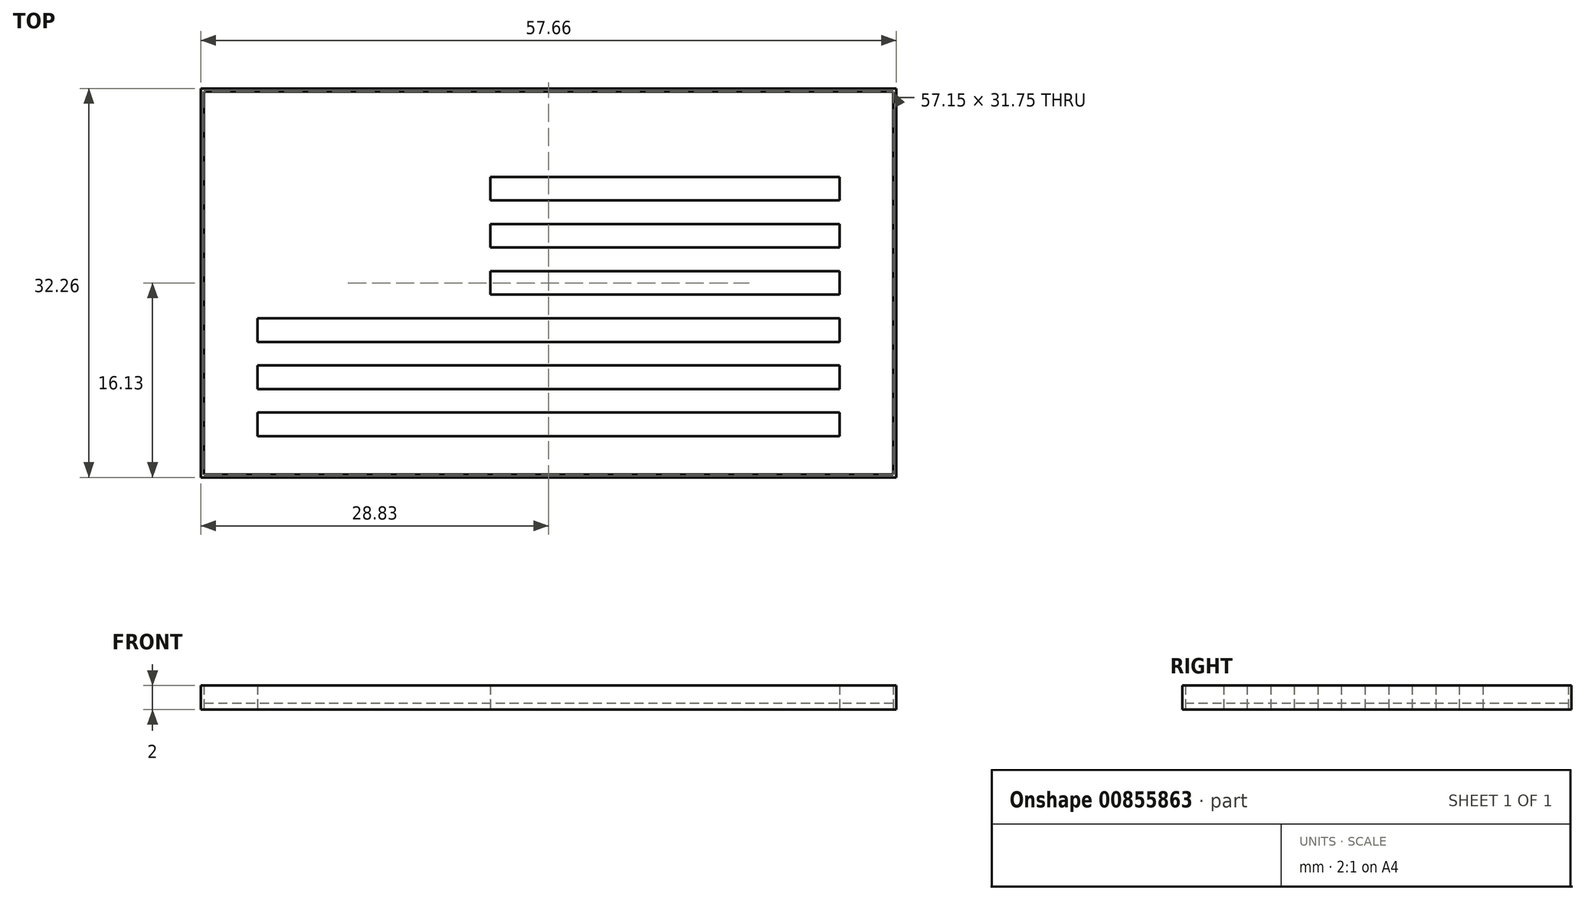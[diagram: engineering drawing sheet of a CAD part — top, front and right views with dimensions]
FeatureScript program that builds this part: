
annotation { "Feature Type Name" : "Feature", "Feature Type Description" : "" }
export const myFeature = defineFeature(function(context is Context, id is Id, definition is map)
    precondition{}
    {
        {
            var Q0;
            Q0=qCreatedBy(makeId("Top.planeOp"),FACE);
            var sketch = newSketch(context, id + "F0", { "sketchPlane" : qUnion([Q0])});
            skLineSegment(sketch, "E0.rect.bottom", {"start": v(24.13, 12.7) * mm, "end": v(-24.13, 12.7) * mm});
            skLineSegment(sketch, "E0.rect.top", {"start": v(24.13, -12.7) * mm, "end": v(-24.13, -12.7) * mm});
            skLineSegment(sketch, "E0.rect.left", {"start": v(24.13, 12.7) * mm, "end": v(24.13, -12.7) * mm});
            skLineSegment(sketch, "E0.rect.right", {"start": v(-24.13, 12.7) * mm, "end": v(-24.13, -12.7) * mm});
            skPoint(sketch, "E0.rect.middle", {"position": v(0, 0) * mm});
            skLineSegment(sketch, "E1.bottom", {"start": v(-24.13, 12.7) * mm, "end": v(-4.83, 12.7) * mm});
            skLineSegment(sketch, "E1.top", {"start": v(-24.13, -0.98) * mm, "end": v(-4.83, -0.98) * mm});
            skLineSegment(sketch, "E1.left", {"start": v(-24.13, 12.7) * mm, "end": v(-24.13, -0.98) * mm});
            skLineSegment(sketch, "E1.right", {"start": v(-4.83, 12.7) * mm, "end": v(-4.83, -0.98) * mm});
            skLineSegment(sketch, "E2.bottom", {"start": v(-4.83, 12.7) * mm, "end": v(24.13, 12.7) * mm});
            skLineSegment(sketch, "E2.top", {"start": v(-4.83, 10.75) * mm, "end": v(24.13, 10.75) * mm});
            skLineSegment(sketch, "E2.left", {"start": v(-4.83, 12.7) * mm, "end": v(-4.83, 10.75) * mm});
            skLineSegment(sketch, "E2.right", {"start": v(24.13, 12.7) * mm, "end": v(24.13, 10.75) * mm});
            skLineSegment(sketch, "E3.MirrorCS", {"start": v(-4.83, 8.8) * mm, "end": v(24.13, 8.8) * mm});
            skLineSegment(sketch, "E4.MirrorCS", {"start": v(-4.83, 6.84) * mm, "end": v(24.13, 6.84) * mm});
            skLineSegment(sketch, "E5.MirrorCS", {"start": v(-4.83, 4.89) * mm, "end": v(24.13, 4.89) * mm});
            skLineSegment(sketch, "E6.MirrorCS", {"start": v(-4.83, 2.93) * mm, "end": v(24.13, 2.93) * mm});
            skLineSegment(sketch, "E7.MirrorCS", {"start": v(-4.83, 0.98) * mm, "end": v(24.13, 0.98) * mm});
            skLineSegment(sketch, "E8.MirrorCS", {"start": v(-4.83, -0.97) * mm, "end": v(24.13, -0.97) * mm});
            skLineSegment(sketch, "E9.bottom", {"start": v(-24.13, -0.98) * mm, "end": v(24.13, -0.98) * mm});
            skLineSegment(sketch, "E9.top", {"start": v(-24.13, -2.93) * mm, "end": v(24.13, -2.93) * mm});
            skLineSegment(sketch, "E9.left", {"start": v(-24.13, -0.98) * mm, "end": v(-24.13, -2.93) * mm});
            skLineSegment(sketch, "E9.right", {"start": v(24.13, -0.98) * mm, "end": v(24.13, -2.93) * mm});
            skLineSegment(sketch, "E10.MirrorCS", {"start": v(-24.13, -4.88) * mm, "end": v(24.13, -4.88) * mm});
            skLineSegment(sketch, "E11.MirrorCS", {"start": v(-24.13, -6.84) * mm, "end": v(24.13, -6.84) * mm});
            skLineSegment(sketch, "E12.MirrorCS", {"start": v(-24.13, -8.8) * mm, "end": v(24.13, -8.8) * mm});
            skLineSegment(sketch, "E13.MirrorCS", {"start": v(-24.13, -10.74) * mm, "end": v(24.13, -10.74) * mm});
            skLineSegment(sketch, "E14.bottom", {"start": v(-24.13, 12.7) * mm, "end": v(-22.53, 12.7) * mm});
            skLineSegment(sketch, "E14.left", {"start": v(-24.13, 12.7) * mm, "end": v(-24.13, 11.33) * mm});
            skPoint(sketch, "E15.cCircle.perimeterSnap0", {"position": v(-22.53, 12.01) * mm});
            skPoint(sketch, "E15.0.startSnap0", {"position": v(-22.53, 12.01) * mm});
            skLineSegment(sketch, "E16", {"start": v(-22.53, 12.12) * mm, "end": v(-22.35, 11.57) * mm});
            skLineSegment(sketch, "E17", {"start": v(-21.78, 11.57) * mm, "end": v(-22.35, 11.57) * mm});
            skLineSegment(sketch, "E18", {"start": v(-23, 10.7) * mm, "end": v(-22.82, 11.24) * mm});
            skLineSegment(sketch, "E19", {"start": v(-23.28, 11.57) * mm, "end": v(-22.82, 11.24) * mm});
            skLineSegment(sketch, "E20", {"start": v(-21.78, 11.57) * mm, "end": v(-22.24, 11.24) * mm});
            skLineSegment(sketch, "E21.trimOffspring", {"start": v(-22.24, 11.24) * mm, "end": v(-22.07, 10.7) * mm});
            skLineSegment(sketch, "E22.trimOffspring", {"start": v(-22.53, 11.03) * mm, "end": v(-23, 10.7) * mm});
            skLineSegment(sketch, "E23.trimOffspring", {"start": v(-22.53, 11.03) * mm, "end": v(-22.07, 10.7) * mm});
            skLineSegment(sketch, "E24.trimOffspring", {"start": v(-22.7, 11.57) * mm, "end": v(-22.53, 12.12) * mm});
            skLineSegment(sketch, "E25.trimOffspring", {"start": v(-22.7, 11.57) * mm, "end": v(-23.28, 11.57) * mm});
            skLineSegment(sketch, "E26.0.1.0", {"start": v(-22.53, 9.37) * mm, "end": v(-22.35, 8.83) * mm});
            skLineSegment(sketch, "E26.0.1.1", {"start": v(-21.78, 8.83) * mm, "end": v(-22.35, 8.83) * mm});
            skLineSegment(sketch, "E26.0.1.2", {"start": v(-21.78, 8.83) * mm, "end": v(-22.24, 8.5) * mm});
            skLineSegment(sketch, "E26.0.1.3", {"start": v(-22.24, 8.5) * mm, "end": v(-22.07, 7.95) * mm});
            skLineSegment(sketch, "E26.0.1.4", {"start": v(-22.53, 8.28) * mm, "end": v(-22.07, 7.95) * mm});
            skLineSegment(sketch, "E26.0.1.5", {"start": v(-22.53, 8.28) * mm, "end": v(-23, 7.95) * mm});
            skLineSegment(sketch, "E26.0.1.6", {"start": v(-23, 7.95) * mm, "end": v(-22.82, 8.5) * mm});
            skLineSegment(sketch, "E26.0.1.7", {"start": v(-23.28, 8.83) * mm, "end": v(-22.82, 8.5) * mm});
            skLineSegment(sketch, "E26.0.1.8", {"start": v(-22.7, 8.83) * mm, "end": v(-22.53, 9.37) * mm});
            skLineSegment(sketch, "E26.0.1.9", {"start": v(-22.7, 8.83) * mm, "end": v(-23.28, 8.83) * mm});
            skLineSegment(sketch, "E26.0.2.0", {"start": v(-22.53, 6.63) * mm, "end": v(-22.35, 6.09) * mm});
            skLineSegment(sketch, "E26.0.2.1", {"start": v(-21.78, 6.09) * mm, "end": v(-22.35, 6.09) * mm});
            skLineSegment(sketch, "E26.0.2.2", {"start": v(-21.78, 6.09) * mm, "end": v(-22.24, 5.75) * mm});
            skLineSegment(sketch, "E26.0.2.3", {"start": v(-22.24, 5.75) * mm, "end": v(-22.07, 5.2) * mm});
            skLineSegment(sketch, "E26.0.2.4", {"start": v(-22.53, 5.54) * mm, "end": v(-22.07, 5.2) * mm});
            skLineSegment(sketch, "E26.0.2.5", {"start": v(-22.53, 5.54) * mm, "end": v(-23, 5.2) * mm});
            skLineSegment(sketch, "E26.0.2.6", {"start": v(-23, 5.2) * mm, "end": v(-22.82, 5.75) * mm});
            skLineSegment(sketch, "E26.0.2.7", {"start": v(-23.28, 6.09) * mm, "end": v(-22.82, 5.75) * mm});
            skLineSegment(sketch, "E26.0.2.8", {"start": v(-22.7, 6.09) * mm, "end": v(-22.53, 6.63) * mm});
            skLineSegment(sketch, "E26.0.2.9", {"start": v(-22.7, 6.09) * mm, "end": v(-23.28, 6.09) * mm});
            skLineSegment(sketch, "E26.0.3.0", {"start": v(-22.53, 3.89) * mm, "end": v(-22.35, 3.34) * mm});
            skLineSegment(sketch, "E26.0.3.1", {"start": v(-21.78, 3.34) * mm, "end": v(-22.35, 3.34) * mm});
            skLineSegment(sketch, "E26.0.3.2", {"start": v(-21.78, 3.34) * mm, "end": v(-22.24, 3) * mm});
            skLineSegment(sketch, "E26.0.3.3", {"start": v(-22.24, 3) * mm, "end": v(-22.07, 2.46) * mm});
            skLineSegment(sketch, "E26.0.3.4", {"start": v(-22.53, 2.8) * mm, "end": v(-22.07, 2.46) * mm});
            skLineSegment(sketch, "E26.0.3.5", {"start": v(-22.53, 2.8) * mm, "end": v(-23, 2.46) * mm});
            skLineSegment(sketch, "E26.0.3.6", {"start": v(-23, 2.46) * mm, "end": v(-22.82, 3) * mm});
            skLineSegment(sketch, "E26.0.3.7", {"start": v(-23.28, 3.34) * mm, "end": v(-22.82, 3) * mm});
            skLineSegment(sketch, "E26.0.3.8", {"start": v(-22.7, 3.34) * mm, "end": v(-22.53, 3.89) * mm});
            skLineSegment(sketch, "E26.0.3.9", {"start": v(-22.7, 3.34) * mm, "end": v(-23.28, 3.34) * mm});
            skLineSegment(sketch, "E26.0.4.0", {"start": v(-22.53, 1.14) * mm, "end": v(-22.35, 0.6) * mm});
            skLineSegment(sketch, "E26.0.4.1", {"start": v(-21.78, 0.6) * mm, "end": v(-22.35, 0.6) * mm});
            skLineSegment(sketch, "E26.0.4.2", {"start": v(-21.78, 0.6) * mm, "end": v(-22.24, 0.26) * mm});
            skLineSegment(sketch, "E26.0.4.3", {"start": v(-22.24, 0.26) * mm, "end": v(-22.07, -0.28) * mm});
            skLineSegment(sketch, "E26.0.4.4", {"start": v(-22.53, 0.05) * mm, "end": v(-22.07, -0.28) * mm});
            skLineSegment(sketch, "E26.0.4.5", {"start": v(-22.53, 0.05) * mm, "end": v(-23, -0.28) * mm});
            skLineSegment(sketch, "E26.0.4.6", {"start": v(-23, -0.28) * mm, "end": v(-22.82, 0.26) * mm});
            skLineSegment(sketch, "E26.0.4.7", {"start": v(-23.28, 0.6) * mm, "end": v(-22.82, 0.26) * mm});
            skLineSegment(sketch, "E26.0.4.8", {"start": v(-22.7, 0.6) * mm, "end": v(-22.53, 1.14) * mm});
            skLineSegment(sketch, "E26.0.4.9", {"start": v(-22.7, 0.6) * mm, "end": v(-23.28, 0.6) * mm});
            skLineSegment(sketch, "E26.1.0.0", {"start": v(-19.33, 12.12) * mm, "end": v(-19.15, 11.57) * mm});
            skLineSegment(sketch, "E26.1.0.1", {"start": v(-18.58, 11.57) * mm, "end": v(-19.15, 11.57) * mm});
            skLineSegment(sketch, "E26.1.0.2", {"start": v(-18.58, 11.57) * mm, "end": v(-19.04, 11.24) * mm});
            skLineSegment(sketch, "E26.1.0.3", {"start": v(-19.04, 11.24) * mm, "end": v(-18.87, 10.7) * mm});
            skLineSegment(sketch, "E26.1.0.4", {"start": v(-19.33, 11.03) * mm, "end": v(-18.87, 10.7) * mm});
            skLineSegment(sketch, "E26.1.0.5", {"start": v(-19.33, 11.03) * mm, "end": v(-19.8, 10.7) * mm});
            skLineSegment(sketch, "E26.1.0.6", {"start": v(-19.8, 10.7) * mm, "end": v(-19.62, 11.24) * mm});
            skLineSegment(sketch, "E26.1.0.7", {"start": v(-20.08, 11.57) * mm, "end": v(-19.62, 11.24) * mm});
            skLineSegment(sketch, "E26.1.0.8", {"start": v(-19.5, 11.57) * mm, "end": v(-19.33, 12.12) * mm});
            skLineSegment(sketch, "E26.1.0.9", {"start": v(-19.5, 11.57) * mm, "end": v(-20.08, 11.57) * mm});
            skLineSegment(sketch, "E26.1.1.0", {"start": v(-19.33, 9.37) * mm, "end": v(-19.15, 8.83) * mm});
            skLineSegment(sketch, "E26.1.1.1", {"start": v(-18.58, 8.83) * mm, "end": v(-19.15, 8.83) * mm});
            skLineSegment(sketch, "E26.1.1.2", {"start": v(-18.58, 8.83) * mm, "end": v(-19.04, 8.5) * mm});
            skLineSegment(sketch, "E26.1.1.3", {"start": v(-19.04, 8.5) * mm, "end": v(-18.87, 7.95) * mm});
            skLineSegment(sketch, "E26.1.1.4", {"start": v(-19.33, 8.28) * mm, "end": v(-18.87, 7.95) * mm});
            skLineSegment(sketch, "E26.1.1.5", {"start": v(-19.33, 8.28) * mm, "end": v(-19.8, 7.95) * mm});
            skLineSegment(sketch, "E26.1.1.6", {"start": v(-19.8, 7.95) * mm, "end": v(-19.62, 8.5) * mm});
            skLineSegment(sketch, "E26.1.1.7", {"start": v(-20.08, 8.83) * mm, "end": v(-19.62, 8.5) * mm});
            skLineSegment(sketch, "E26.1.1.8", {"start": v(-19.5, 8.83) * mm, "end": v(-19.33, 9.37) * mm});
            skLineSegment(sketch, "E26.1.1.9", {"start": v(-19.5, 8.83) * mm, "end": v(-20.08, 8.83) * mm});
            skLineSegment(sketch, "E26.1.2.0", {"start": v(-19.33, 6.63) * mm, "end": v(-19.15, 6.09) * mm});
            skLineSegment(sketch, "E26.1.2.1", {"start": v(-18.58, 6.09) * mm, "end": v(-19.15, 6.09) * mm});
            skLineSegment(sketch, "E26.1.2.2", {"start": v(-18.58, 6.09) * mm, "end": v(-19.04, 5.75) * mm});
            skLineSegment(sketch, "E26.1.2.3", {"start": v(-19.04, 5.75) * mm, "end": v(-18.87, 5.2) * mm});
            skLineSegment(sketch, "E26.1.2.4", {"start": v(-19.33, 5.54) * mm, "end": v(-18.87, 5.2) * mm});
            skLineSegment(sketch, "E26.1.2.5", {"start": v(-19.33, 5.54) * mm, "end": v(-19.8, 5.2) * mm});
            skLineSegment(sketch, "E26.1.2.6", {"start": v(-19.8, 5.2) * mm, "end": v(-19.62, 5.75) * mm});
            skLineSegment(sketch, "E26.1.2.7", {"start": v(-20.08, 6.09) * mm, "end": v(-19.62, 5.75) * mm});
            skLineSegment(sketch, "E26.1.2.8", {"start": v(-19.5, 6.09) * mm, "end": v(-19.33, 6.63) * mm});
            skLineSegment(sketch, "E26.1.2.9", {"start": v(-19.5, 6.09) * mm, "end": v(-20.08, 6.09) * mm});
            skLineSegment(sketch, "E26.1.3.0", {"start": v(-19.33, 3.89) * mm, "end": v(-19.15, 3.34) * mm});
            skLineSegment(sketch, "E26.1.3.1", {"start": v(-18.58, 3.34) * mm, "end": v(-19.15, 3.34) * mm});
            skLineSegment(sketch, "E26.1.3.2", {"start": v(-18.58, 3.34) * mm, "end": v(-19.04, 3) * mm});
            skLineSegment(sketch, "E26.1.3.3", {"start": v(-19.04, 3) * mm, "end": v(-18.87, 2.46) * mm});
            skLineSegment(sketch, "E26.1.3.4", {"start": v(-19.33, 2.8) * mm, "end": v(-18.87, 2.46) * mm});
            skLineSegment(sketch, "E26.1.3.5", {"start": v(-19.33, 2.8) * mm, "end": v(-19.8, 2.46) * mm});
            skLineSegment(sketch, "E26.1.3.6", {"start": v(-19.8, 2.46) * mm, "end": v(-19.62, 3) * mm});
            skLineSegment(sketch, "E26.1.3.7", {"start": v(-20.08, 3.34) * mm, "end": v(-19.62, 3) * mm});
            skLineSegment(sketch, "E26.1.3.8", {"start": v(-19.5, 3.34) * mm, "end": v(-19.33, 3.89) * mm});
            skLineSegment(sketch, "E26.1.3.9", {"start": v(-19.5, 3.34) * mm, "end": v(-20.08, 3.34) * mm});
            skLineSegment(sketch, "E26.1.4.0", {"start": v(-19.33, 1.14) * mm, "end": v(-19.15, 0.6) * mm});
            skLineSegment(sketch, "E26.1.4.1", {"start": v(-18.58, 0.6) * mm, "end": v(-19.15, 0.6) * mm});
            skLineSegment(sketch, "E26.1.4.2", {"start": v(-18.58, 0.6) * mm, "end": v(-19.04, 0.26) * mm});
            skLineSegment(sketch, "E26.1.4.3", {"start": v(-19.04, 0.26) * mm, "end": v(-18.87, -0.28) * mm});
            skLineSegment(sketch, "E26.1.4.4", {"start": v(-19.33, 0.05) * mm, "end": v(-18.87, -0.28) * mm});
            skLineSegment(sketch, "E26.1.4.5", {"start": v(-19.33, 0.05) * mm, "end": v(-19.8, -0.28) * mm});
            skLineSegment(sketch, "E26.1.4.6", {"start": v(-19.8, -0.28) * mm, "end": v(-19.62, 0.26) * mm});
            skLineSegment(sketch, "E26.1.4.7", {"start": v(-20.08, 0.6) * mm, "end": v(-19.62, 0.26) * mm});
            skLineSegment(sketch, "E26.1.4.8", {"start": v(-19.5, 0.6) * mm, "end": v(-19.33, 1.14) * mm});
            skLineSegment(sketch, "E26.1.4.9", {"start": v(-19.5, 0.6) * mm, "end": v(-20.08, 0.6) * mm});
            skLineSegment(sketch, "E26.2.0.0", {"start": v(-16.13, 12.12) * mm, "end": v(-15.95, 11.57) * mm});
            skLineSegment(sketch, "E26.2.0.1", {"start": v(-15.38, 11.57) * mm, "end": v(-15.95, 11.57) * mm});
            skLineSegment(sketch, "E26.2.0.2", {"start": v(-15.38, 11.57) * mm, "end": v(-15.84, 11.24) * mm});
            skLineSegment(sketch, "E26.2.0.3", {"start": v(-15.84, 11.24) * mm, "end": v(-15.67, 10.7) * mm});
            skLineSegment(sketch, "E26.2.0.4", {"start": v(-16.13, 11.03) * mm, "end": v(-15.67, 10.7) * mm});
            skLineSegment(sketch, "E26.2.0.5", {"start": v(-16.13, 11.03) * mm, "end": v(-16.6, 10.7) * mm});
            skLineSegment(sketch, "E26.2.0.6", {"start": v(-16.6, 10.7) * mm, "end": v(-16.42, 11.24) * mm});
            skLineSegment(sketch, "E26.2.0.7", {"start": v(-16.88, 11.57) * mm, "end": v(-16.42, 11.24) * mm});
            skLineSegment(sketch, "E26.2.0.8", {"start": v(-16.3, 11.57) * mm, "end": v(-16.13, 12.12) * mm});
            skLineSegment(sketch, "E26.2.0.9", {"start": v(-16.3, 11.57) * mm, "end": v(-16.88, 11.57) * mm});
            skLineSegment(sketch, "E26.2.1.0", {"start": v(-16.13, 9.37) * mm, "end": v(-15.95, 8.83) * mm});
            skLineSegment(sketch, "E26.2.1.1", {"start": v(-15.38, 8.83) * mm, "end": v(-15.95, 8.83) * mm});
            skLineSegment(sketch, "E26.2.1.2", {"start": v(-15.38, 8.83) * mm, "end": v(-15.84, 8.5) * mm});
            skLineSegment(sketch, "E26.2.1.3", {"start": v(-15.84, 8.5) * mm, "end": v(-15.67, 7.95) * mm});
            skLineSegment(sketch, "E26.2.1.4", {"start": v(-16.13, 8.28) * mm, "end": v(-15.67, 7.95) * mm});
            skLineSegment(sketch, "E26.2.1.5", {"start": v(-16.13, 8.28) * mm, "end": v(-16.6, 7.95) * mm});
            skLineSegment(sketch, "E26.2.1.6", {"start": v(-16.6, 7.95) * mm, "end": v(-16.42, 8.5) * mm});
            skLineSegment(sketch, "E26.2.1.7", {"start": v(-16.88, 8.83) * mm, "end": v(-16.42, 8.5) * mm});
            skLineSegment(sketch, "E26.2.1.8", {"start": v(-16.3, 8.83) * mm, "end": v(-16.13, 9.37) * mm});
            skLineSegment(sketch, "E26.2.1.9", {"start": v(-16.3, 8.83) * mm, "end": v(-16.88, 8.83) * mm});
            skLineSegment(sketch, "E26.2.2.0", {"start": v(-16.13, 6.63) * mm, "end": v(-15.95, 6.09) * mm});
            skLineSegment(sketch, "E26.2.2.1", {"start": v(-15.38, 6.09) * mm, "end": v(-15.95, 6.09) * mm});
            skLineSegment(sketch, "E26.2.2.2", {"start": v(-15.38, 6.09) * mm, "end": v(-15.84, 5.75) * mm});
            skLineSegment(sketch, "E26.2.2.3", {"start": v(-15.84, 5.75) * mm, "end": v(-15.67, 5.2) * mm});
            skLineSegment(sketch, "E26.2.2.4", {"start": v(-16.13, 5.54) * mm, "end": v(-15.67, 5.2) * mm});
            skLineSegment(sketch, "E26.2.2.5", {"start": v(-16.13, 5.54) * mm, "end": v(-16.6, 5.2) * mm});
            skLineSegment(sketch, "E26.2.2.6", {"start": v(-16.6, 5.2) * mm, "end": v(-16.42, 5.75) * mm});
            skLineSegment(sketch, "E26.2.2.7", {"start": v(-16.88, 6.09) * mm, "end": v(-16.42, 5.75) * mm});
            skLineSegment(sketch, "E26.2.2.8", {"start": v(-16.3, 6.09) * mm, "end": v(-16.13, 6.63) * mm});
            skLineSegment(sketch, "E26.2.2.9", {"start": v(-16.3, 6.09) * mm, "end": v(-16.88, 6.09) * mm});
            skLineSegment(sketch, "E26.2.3.0", {"start": v(-16.13, 3.89) * mm, "end": v(-15.95, 3.34) * mm});
            skLineSegment(sketch, "E26.2.3.1", {"start": v(-15.38, 3.34) * mm, "end": v(-15.95, 3.34) * mm});
            skLineSegment(sketch, "E26.2.3.2", {"start": v(-15.38, 3.34) * mm, "end": v(-15.84, 3) * mm});
            skLineSegment(sketch, "E26.2.3.3", {"start": v(-15.84, 3) * mm, "end": v(-15.67, 2.46) * mm});
            skLineSegment(sketch, "E26.2.3.4", {"start": v(-16.13, 2.8) * mm, "end": v(-15.67, 2.46) * mm});
            skLineSegment(sketch, "E26.2.3.5", {"start": v(-16.13, 2.8) * mm, "end": v(-16.6, 2.46) * mm});
            skLineSegment(sketch, "E26.2.3.6", {"start": v(-16.6, 2.46) * mm, "end": v(-16.42, 3) * mm});
            skLineSegment(sketch, "E26.2.3.7", {"start": v(-16.88, 3.34) * mm, "end": v(-16.42, 3) * mm});
            skLineSegment(sketch, "E26.2.3.8", {"start": v(-16.3, 3.34) * mm, "end": v(-16.13, 3.89) * mm});
            skLineSegment(sketch, "E26.2.3.9", {"start": v(-16.3, 3.34) * mm, "end": v(-16.88, 3.34) * mm});
            skLineSegment(sketch, "E26.2.4.0", {"start": v(-16.13, 1.14) * mm, "end": v(-15.95, 0.6) * mm});
            skLineSegment(sketch, "E26.2.4.1", {"start": v(-15.38, 0.6) * mm, "end": v(-15.95, 0.6) * mm});
            skLineSegment(sketch, "E26.2.4.2", {"start": v(-15.38, 0.6) * mm, "end": v(-15.84, 0.26) * mm});
            skLineSegment(sketch, "E26.2.4.3", {"start": v(-15.84, 0.26) * mm, "end": v(-15.67, -0.28) * mm});
            skLineSegment(sketch, "E26.2.4.4", {"start": v(-16.13, 0.05) * mm, "end": v(-15.67, -0.28) * mm});
            skLineSegment(sketch, "E26.2.4.5", {"start": v(-16.13, 0.05) * mm, "end": v(-16.6, -0.28) * mm});
            skLineSegment(sketch, "E26.2.4.6", {"start": v(-16.6, -0.28) * mm, "end": v(-16.42, 0.26) * mm});
            skLineSegment(sketch, "E26.2.4.7", {"start": v(-16.88, 0.6) * mm, "end": v(-16.42, 0.26) * mm});
            skLineSegment(sketch, "E26.2.4.8", {"start": v(-16.3, 0.6) * mm, "end": v(-16.13, 1.14) * mm});
            skLineSegment(sketch, "E26.2.4.9", {"start": v(-16.3, 0.6) * mm, "end": v(-16.88, 0.6) * mm});
            skLineSegment(sketch, "E26.3.0.0", {"start": v(-12.93, 12.12) * mm, "end": v(-12.75, 11.57) * mm});
            skLineSegment(sketch, "E26.3.0.1", {"start": v(-12.18, 11.57) * mm, "end": v(-12.75, 11.57) * mm});
            skLineSegment(sketch, "E26.3.0.2", {"start": v(-12.18, 11.57) * mm, "end": v(-12.64, 11.24) * mm});
            skLineSegment(sketch, "E26.3.0.3", {"start": v(-12.64, 11.24) * mm, "end": v(-12.47, 10.7) * mm});
            skLineSegment(sketch, "E26.3.0.4", {"start": v(-12.93, 11.03) * mm, "end": v(-12.47, 10.7) * mm});
            skLineSegment(sketch, "E26.3.0.5", {"start": v(-12.93, 11.03) * mm, "end": v(-13.4, 10.7) * mm});
            skLineSegment(sketch, "E26.3.0.6", {"start": v(-13.4, 10.7) * mm, "end": v(-13.21, 11.24) * mm});
            skLineSegment(sketch, "E26.3.0.7", {"start": v(-13.68, 11.57) * mm, "end": v(-13.21, 11.24) * mm});
            skLineSegment(sketch, "E26.3.0.8", {"start": v(-13.1, 11.57) * mm, "end": v(-12.93, 12.12) * mm});
            skLineSegment(sketch, "E26.3.0.9", {"start": v(-13.1, 11.57) * mm, "end": v(-13.68, 11.57) * mm});
            skLineSegment(sketch, "E26.3.1.0", {"start": v(-12.93, 9.37) * mm, "end": v(-12.75, 8.83) * mm});
            skLineSegment(sketch, "E26.3.1.1", {"start": v(-12.18, 8.83) * mm, "end": v(-12.75, 8.83) * mm});
            skLineSegment(sketch, "E26.3.1.2", {"start": v(-12.18, 8.83) * mm, "end": v(-12.64, 8.5) * mm});
            skLineSegment(sketch, "E26.3.1.3", {"start": v(-12.64, 8.5) * mm, "end": v(-12.47, 7.95) * mm});
            skLineSegment(sketch, "E26.3.1.4", {"start": v(-12.93, 8.28) * mm, "end": v(-12.47, 7.95) * mm});
            skLineSegment(sketch, "E26.3.1.5", {"start": v(-12.93, 8.28) * mm, "end": v(-13.4, 7.95) * mm});
            skLineSegment(sketch, "E26.3.1.6", {"start": v(-13.4, 7.95) * mm, "end": v(-13.21, 8.5) * mm});
            skLineSegment(sketch, "E26.3.1.7", {"start": v(-13.68, 8.83) * mm, "end": v(-13.21, 8.5) * mm});
            skLineSegment(sketch, "E26.3.1.8", {"start": v(-13.1, 8.83) * mm, "end": v(-12.93, 9.37) * mm});
            skLineSegment(sketch, "E26.3.1.9", {"start": v(-13.1, 8.83) * mm, "end": v(-13.68, 8.83) * mm});
            skLineSegment(sketch, "E26.3.2.0", {"start": v(-12.93, 6.63) * mm, "end": v(-12.75, 6.09) * mm});
            skLineSegment(sketch, "E26.3.2.1", {"start": v(-12.18, 6.09) * mm, "end": v(-12.75, 6.09) * mm});
            skLineSegment(sketch, "E26.3.2.2", {"start": v(-12.18, 6.09) * mm, "end": v(-12.64, 5.75) * mm});
            skLineSegment(sketch, "E26.3.2.3", {"start": v(-12.64, 5.75) * mm, "end": v(-12.47, 5.2) * mm});
            skLineSegment(sketch, "E26.3.2.4", {"start": v(-12.93, 5.54) * mm, "end": v(-12.47, 5.2) * mm});
            skLineSegment(sketch, "E26.3.2.5", {"start": v(-12.93, 5.54) * mm, "end": v(-13.4, 5.2) * mm});
            skLineSegment(sketch, "E26.3.2.6", {"start": v(-13.4, 5.2) * mm, "end": v(-13.21, 5.75) * mm});
            skLineSegment(sketch, "E26.3.2.7", {"start": v(-13.68, 6.09) * mm, "end": v(-13.21, 5.75) * mm});
            skLineSegment(sketch, "E26.3.2.8", {"start": v(-13.1, 6.09) * mm, "end": v(-12.93, 6.63) * mm});
            skLineSegment(sketch, "E26.3.2.9", {"start": v(-13.1, 6.09) * mm, "end": v(-13.68, 6.09) * mm});
            skLineSegment(sketch, "E26.3.3.0", {"start": v(-12.93, 3.89) * mm, "end": v(-12.75, 3.34) * mm});
            skLineSegment(sketch, "E26.3.3.1", {"start": v(-12.18, 3.34) * mm, "end": v(-12.75, 3.34) * mm});
            skLineSegment(sketch, "E26.3.3.2", {"start": v(-12.18, 3.34) * mm, "end": v(-12.64, 3) * mm});
            skLineSegment(sketch, "E26.3.3.3", {"start": v(-12.64, 3) * mm, "end": v(-12.47, 2.46) * mm});
            skLineSegment(sketch, "E26.3.3.4", {"start": v(-12.93, 2.8) * mm, "end": v(-12.47, 2.46) * mm});
            skLineSegment(sketch, "E26.3.3.5", {"start": v(-12.93, 2.8) * mm, "end": v(-13.4, 2.46) * mm});
            skLineSegment(sketch, "E26.3.3.6", {"start": v(-13.4, 2.46) * mm, "end": v(-13.21, 3) * mm});
            skLineSegment(sketch, "E26.3.3.7", {"start": v(-13.68, 3.34) * mm, "end": v(-13.21, 3) * mm});
            skLineSegment(sketch, "E26.3.3.8", {"start": v(-13.1, 3.34) * mm, "end": v(-12.93, 3.89) * mm});
            skLineSegment(sketch, "E26.3.3.9", {"start": v(-13.1, 3.34) * mm, "end": v(-13.68, 3.34) * mm});
            skLineSegment(sketch, "E26.3.4.0", {"start": v(-12.93, 1.14) * mm, "end": v(-12.75, 0.6) * mm});
            skLineSegment(sketch, "E26.3.4.1", {"start": v(-12.18, 0.6) * mm, "end": v(-12.75, 0.6) * mm});
            skLineSegment(sketch, "E26.3.4.2", {"start": v(-12.18, 0.6) * mm, "end": v(-12.64, 0.26) * mm});
            skLineSegment(sketch, "E26.3.4.3", {"start": v(-12.64, 0.26) * mm, "end": v(-12.47, -0.28) * mm});
            skLineSegment(sketch, "E26.3.4.4", {"start": v(-12.93, 0.05) * mm, "end": v(-12.47, -0.28) * mm});
            skLineSegment(sketch, "E26.3.4.5", {"start": v(-12.93, 0.05) * mm, "end": v(-13.4, -0.28) * mm});
            skLineSegment(sketch, "E26.3.4.6", {"start": v(-13.4, -0.28) * mm, "end": v(-13.21, 0.26) * mm});
            skLineSegment(sketch, "E26.3.4.7", {"start": v(-13.68, 0.6) * mm, "end": v(-13.21, 0.26) * mm});
            skLineSegment(sketch, "E26.3.4.8", {"start": v(-13.1, 0.6) * mm, "end": v(-12.93, 1.14) * mm});
            skLineSegment(sketch, "E26.3.4.9", {"start": v(-13.1, 0.6) * mm, "end": v(-13.68, 0.6) * mm});
            skLineSegment(sketch, "E26.4.0.0", {"start": v(-9.73, 12.12) * mm, "end": v(-9.55, 11.57) * mm});
            skLineSegment(sketch, "E26.4.0.1", {"start": v(-8.98, 11.57) * mm, "end": v(-9.55, 11.57) * mm});
            skLineSegment(sketch, "E26.4.0.2", {"start": v(-8.98, 11.57) * mm, "end": v(-9.44, 11.24) * mm});
            skLineSegment(sketch, "E26.4.0.3", {"start": v(-9.44, 11.24) * mm, "end": v(-9.27, 10.7) * mm});
            skLineSegment(sketch, "E26.4.0.4", {"start": v(-9.73, 11.03) * mm, "end": v(-9.27, 10.7) * mm});
            skLineSegment(sketch, "E26.4.0.5", {"start": v(-9.73, 11.03) * mm, "end": v(-10.2, 10.7) * mm});
            skLineSegment(sketch, "E26.4.0.6", {"start": v(-10.2, 10.7) * mm, "end": v(-10.01, 11.24) * mm});
            skLineSegment(sketch, "E26.4.0.7", {"start": v(-10.48, 11.57) * mm, "end": v(-10.01, 11.24) * mm});
            skLineSegment(sketch, "E26.4.0.8", {"start": v(-9.9, 11.57) * mm, "end": v(-9.73, 12.12) * mm});
            skLineSegment(sketch, "E26.4.0.9", {"start": v(-9.9, 11.57) * mm, "end": v(-10.48, 11.57) * mm});
            skLineSegment(sketch, "E26.4.1.0", {"start": v(-9.73, 9.37) * mm, "end": v(-9.55, 8.83) * mm});
            skLineSegment(sketch, "E26.4.1.1", {"start": v(-8.98, 8.83) * mm, "end": v(-9.55, 8.83) * mm});
            skLineSegment(sketch, "E26.4.1.2", {"start": v(-8.98, 8.83) * mm, "end": v(-9.44, 8.5) * mm});
            skLineSegment(sketch, "E26.4.1.3", {"start": v(-9.44, 8.5) * mm, "end": v(-9.27, 7.95) * mm});
            skLineSegment(sketch, "E26.4.1.4", {"start": v(-9.73, 8.28) * mm, "end": v(-9.27, 7.95) * mm});
            skLineSegment(sketch, "E26.4.1.5", {"start": v(-9.73, 8.28) * mm, "end": v(-10.2, 7.95) * mm});
            skLineSegment(sketch, "E26.4.1.6", {"start": v(-10.2, 7.95) * mm, "end": v(-10.01, 8.5) * mm});
            skLineSegment(sketch, "E26.4.1.7", {"start": v(-10.48, 8.83) * mm, "end": v(-10.01, 8.5) * mm});
            skLineSegment(sketch, "E26.4.1.8", {"start": v(-9.9, 8.83) * mm, "end": v(-9.73, 9.37) * mm});
            skLineSegment(sketch, "E26.4.1.9", {"start": v(-9.9, 8.83) * mm, "end": v(-10.48, 8.83) * mm});
            skLineSegment(sketch, "E26.4.2.0", {"start": v(-9.73, 6.63) * mm, "end": v(-9.55, 6.09) * mm});
            skLineSegment(sketch, "E26.4.2.1", {"start": v(-8.98, 6.09) * mm, "end": v(-9.55, 6.09) * mm});
            skLineSegment(sketch, "E26.4.2.2", {"start": v(-8.98, 6.09) * mm, "end": v(-9.44, 5.75) * mm});
            skLineSegment(sketch, "E26.4.2.3", {"start": v(-9.44, 5.75) * mm, "end": v(-9.27, 5.2) * mm});
            skLineSegment(sketch, "E26.4.2.4", {"start": v(-9.73, 5.54) * mm, "end": v(-9.27, 5.2) * mm});
            skLineSegment(sketch, "E26.4.2.5", {"start": v(-9.73, 5.54) * mm, "end": v(-10.2, 5.2) * mm});
            skLineSegment(sketch, "E26.4.2.6", {"start": v(-10.2, 5.2) * mm, "end": v(-10.01, 5.75) * mm});
            skLineSegment(sketch, "E26.4.2.7", {"start": v(-10.48, 6.09) * mm, "end": v(-10.01, 5.75) * mm});
            skLineSegment(sketch, "E26.4.2.8", {"start": v(-9.9, 6.09) * mm, "end": v(-9.73, 6.63) * mm});
            skLineSegment(sketch, "E26.4.2.9", {"start": v(-9.9, 6.09) * mm, "end": v(-10.48, 6.09) * mm});
            skLineSegment(sketch, "E26.4.3.0", {"start": v(-9.73, 3.89) * mm, "end": v(-9.55, 3.34) * mm});
            skLineSegment(sketch, "E26.4.3.1", {"start": v(-8.98, 3.34) * mm, "end": v(-9.55, 3.34) * mm});
            skLineSegment(sketch, "E26.4.3.2", {"start": v(-8.98, 3.34) * mm, "end": v(-9.44, 3) * mm});
            skLineSegment(sketch, "E26.4.3.3", {"start": v(-9.44, 3) * mm, "end": v(-9.27, 2.46) * mm});
            skLineSegment(sketch, "E26.4.3.4", {"start": v(-9.73, 2.8) * mm, "end": v(-9.27, 2.46) * mm});
            skLineSegment(sketch, "E26.4.3.5", {"start": v(-9.73, 2.8) * mm, "end": v(-10.2, 2.46) * mm});
            skLineSegment(sketch, "E26.4.3.6", {"start": v(-10.2, 2.46) * mm, "end": v(-10.01, 3) * mm});
            skLineSegment(sketch, "E26.4.3.7", {"start": v(-10.48, 3.34) * mm, "end": v(-10.01, 3) * mm});
            skLineSegment(sketch, "E26.4.3.8", {"start": v(-9.9, 3.34) * mm, "end": v(-9.73, 3.89) * mm});
            skLineSegment(sketch, "E26.4.3.9", {"start": v(-9.9, 3.34) * mm, "end": v(-10.48, 3.34) * mm});
            skLineSegment(sketch, "E26.4.4.0", {"start": v(-9.73, 1.14) * mm, "end": v(-9.55, 0.6) * mm});
            skLineSegment(sketch, "E26.4.4.1", {"start": v(-8.98, 0.6) * mm, "end": v(-9.55, 0.6) * mm});
            skLineSegment(sketch, "E26.4.4.2", {"start": v(-8.98, 0.6) * mm, "end": v(-9.44, 0.26) * mm});
            skLineSegment(sketch, "E26.4.4.3", {"start": v(-9.44, 0.26) * mm, "end": v(-9.27, -0.28) * mm});
            skLineSegment(sketch, "E26.4.4.4", {"start": v(-9.73, 0.05) * mm, "end": v(-9.27, -0.28) * mm});
            skLineSegment(sketch, "E26.4.4.5", {"start": v(-9.73, 0.05) * mm, "end": v(-10.2, -0.28) * mm});
            skLineSegment(sketch, "E26.4.4.6", {"start": v(-10.2, -0.28) * mm, "end": v(-10.01, 0.26) * mm});
            skLineSegment(sketch, "E26.4.4.7", {"start": v(-10.48, 0.6) * mm, "end": v(-10.01, 0.26) * mm});
            skLineSegment(sketch, "E26.4.4.8", {"start": v(-9.9, 0.6) * mm, "end": v(-9.73, 1.14) * mm});
            skLineSegment(sketch, "E26.4.4.9", {"start": v(-9.9, 0.6) * mm, "end": v(-10.48, 0.6) * mm});
            skLineSegment(sketch, "E26.5.0.0", {"start": v(-6.53, 12.12) * mm, "end": v(-6.35, 11.57) * mm});
            skLineSegment(sketch, "E26.5.0.1", {"start": v(-5.78, 11.57) * mm, "end": v(-6.35, 11.57) * mm});
            skLineSegment(sketch, "E26.5.0.2", {"start": v(-5.78, 11.57) * mm, "end": v(-6.24, 11.24) * mm});
            skLineSegment(sketch, "E26.5.0.3", {"start": v(-6.24, 11.24) * mm, "end": v(-6.06, 10.7) * mm});
            skLineSegment(sketch, "E26.5.0.4", {"start": v(-6.53, 11.03) * mm, "end": v(-6.06, 10.7) * mm});
            skLineSegment(sketch, "E26.5.0.5", {"start": v(-6.53, 11.03) * mm, "end": v(-7, 10.7) * mm});
            skLineSegment(sketch, "E26.5.0.6", {"start": v(-7, 10.7) * mm, "end": v(-6.81, 11.24) * mm});
            skLineSegment(sketch, "E26.5.0.7", {"start": v(-7.28, 11.57) * mm, "end": v(-6.81, 11.24) * mm});
            skLineSegment(sketch, "E26.5.0.8", {"start": v(-6.7, 11.57) * mm, "end": v(-6.53, 12.12) * mm});
            skLineSegment(sketch, "E26.5.0.9", {"start": v(-6.7, 11.57) * mm, "end": v(-7.28, 11.57) * mm});
            skLineSegment(sketch, "E26.5.1.0", {"start": v(-6.53, 9.37) * mm, "end": v(-6.35, 8.83) * mm});
            skLineSegment(sketch, "E26.5.1.1", {"start": v(-5.78, 8.83) * mm, "end": v(-6.35, 8.83) * mm});
            skLineSegment(sketch, "E26.5.1.2", {"start": v(-5.78, 8.83) * mm, "end": v(-6.24, 8.5) * mm});
            skLineSegment(sketch, "E26.5.1.3", {"start": v(-6.24, 8.5) * mm, "end": v(-6.06, 7.95) * mm});
            skLineSegment(sketch, "E26.5.1.4", {"start": v(-6.53, 8.28) * mm, "end": v(-6.06, 7.95) * mm});
            skLineSegment(sketch, "E26.5.1.5", {"start": v(-6.53, 8.28) * mm, "end": v(-7, 7.95) * mm});
            skLineSegment(sketch, "E26.5.1.6", {"start": v(-7, 7.95) * mm, "end": v(-6.81, 8.5) * mm});
            skLineSegment(sketch, "E26.5.1.7", {"start": v(-7.28, 8.83) * mm, "end": v(-6.81, 8.5) * mm});
            skLineSegment(sketch, "E26.5.1.8", {"start": v(-6.7, 8.83) * mm, "end": v(-6.53, 9.37) * mm});
            skLineSegment(sketch, "E26.5.1.9", {"start": v(-6.7, 8.83) * mm, "end": v(-7.28, 8.83) * mm});
            skLineSegment(sketch, "E26.5.2.0", {"start": v(-6.53, 6.63) * mm, "end": v(-6.35, 6.09) * mm});
            skLineSegment(sketch, "E26.5.2.1", {"start": v(-5.78, 6.09) * mm, "end": v(-6.35, 6.09) * mm});
            skLineSegment(sketch, "E26.5.2.2", {"start": v(-5.78, 6.09) * mm, "end": v(-6.24, 5.75) * mm});
            skLineSegment(sketch, "E26.5.2.3", {"start": v(-6.24, 5.75) * mm, "end": v(-6.06, 5.2) * mm});
            skLineSegment(sketch, "E26.5.2.4", {"start": v(-6.53, 5.54) * mm, "end": v(-6.06, 5.2) * mm});
            skLineSegment(sketch, "E26.5.2.5", {"start": v(-6.53, 5.54) * mm, "end": v(-7, 5.2) * mm});
            skLineSegment(sketch, "E26.5.2.6", {"start": v(-7, 5.2) * mm, "end": v(-6.81, 5.75) * mm});
            skLineSegment(sketch, "E26.5.2.7", {"start": v(-7.28, 6.09) * mm, "end": v(-6.81, 5.75) * mm});
            skLineSegment(sketch, "E26.5.2.8", {"start": v(-6.7, 6.09) * mm, "end": v(-6.53, 6.63) * mm});
            skLineSegment(sketch, "E26.5.2.9", {"start": v(-6.7, 6.09) * mm, "end": v(-7.28, 6.09) * mm});
            skLineSegment(sketch, "E26.5.3.0", {"start": v(-6.53, 3.89) * mm, "end": v(-6.35, 3.34) * mm});
            skLineSegment(sketch, "E26.5.3.1", {"start": v(-5.78, 3.34) * mm, "end": v(-6.35, 3.34) * mm});
            skLineSegment(sketch, "E26.5.3.2", {"start": v(-5.78, 3.34) * mm, "end": v(-6.24, 3) * mm});
            skLineSegment(sketch, "E26.5.3.3", {"start": v(-6.24, 3) * mm, "end": v(-6.06, 2.46) * mm});
            skLineSegment(sketch, "E26.5.3.4", {"start": v(-6.53, 2.8) * mm, "end": v(-6.06, 2.46) * mm});
            skLineSegment(sketch, "E26.5.3.5", {"start": v(-6.53, 2.8) * mm, "end": v(-7, 2.46) * mm});
            skLineSegment(sketch, "E26.5.3.6", {"start": v(-7, 2.46) * mm, "end": v(-6.81, 3) * mm});
            skLineSegment(sketch, "E26.5.3.7", {"start": v(-7.28, 3.34) * mm, "end": v(-6.81, 3) * mm});
            skLineSegment(sketch, "E26.5.3.8", {"start": v(-6.7, 3.34) * mm, "end": v(-6.53, 3.89) * mm});
            skLineSegment(sketch, "E26.5.3.9", {"start": v(-6.7, 3.34) * mm, "end": v(-7.28, 3.34) * mm});
            skLineSegment(sketch, "E26.5.4.0", {"start": v(-6.53, 1.14) * mm, "end": v(-6.35, 0.6) * mm});
            skLineSegment(sketch, "E26.5.4.1", {"start": v(-5.78, 0.6) * mm, "end": v(-6.35, 0.6) * mm});
            skLineSegment(sketch, "E26.5.4.2", {"start": v(-5.78, 0.6) * mm, "end": v(-6.24, 0.26) * mm});
            skLineSegment(sketch, "E26.5.4.3", {"start": v(-6.24, 0.26) * mm, "end": v(-6.06, -0.28) * mm});
            skLineSegment(sketch, "E26.5.4.4", {"start": v(-6.53, 0.05) * mm, "end": v(-6.06, -0.28) * mm});
            skLineSegment(sketch, "E26.5.4.5", {"start": v(-6.53, 0.05) * mm, "end": v(-7, -0.28) * mm});
            skLineSegment(sketch, "E26.5.4.6", {"start": v(-7, -0.28) * mm, "end": v(-6.81, 0.26) * mm});
            skLineSegment(sketch, "E26.5.4.7", {"start": v(-7.28, 0.6) * mm, "end": v(-6.81, 0.26) * mm});
            skLineSegment(sketch, "E26.5.4.8", {"start": v(-6.7, 0.6) * mm, "end": v(-6.53, 1.14) * mm});
            skLineSegment(sketch, "E26.5.4.9", {"start": v(-6.7, 0.6) * mm, "end": v(-7.28, 0.6) * mm});
            skLineSegment(sketch, "E26.direction1", {"start": v(-22.35, 11.57) * mm, "end": v(-19.15, 11.57) * mm, "construction": true});
            skLineSegment(sketch, "E26.direction2", {"start": v(-22.35, 11.57) * mm, "end": v(-22.35, 8.83) * mm, "construction": true});
            skPoint(sketch, "E27.cCircle.perimeterSnap0", {"position": v(-20.93, 10.64) * mm});
            skPoint(sketch, "E27.0.startSnap0", {"position": v(-20.93, 10.64) * mm});
            skLineSegment(sketch, "E28", {"start": v(-20.93, 10.75) * mm, "end": v(-20.75, 10.2) * mm});
            skLineSegment(sketch, "E29", {"start": v(-21.68, 10.2) * mm, "end": v(-21.1, 10.2) * mm});
            skLineSegment(sketch, "E30", {"start": v(-21.4, 9.32) * mm, "end": v(-20.93, 9.66) * mm});
            skLineSegment(sketch, "E31", {"start": v(-21.4, 9.32) * mm, "end": v(-21.22, 9.86) * mm});
            skLineSegment(sketch, "E32", {"start": v(-20.47, 9.32) * mm, "end": v(-20.93, 9.66) * mm});
            skLineSegment(sketch, "E33.trimOffspring", {"start": v(-20.64, 9.86) * mm, "end": v(-20.47, 9.32) * mm});
            skLineSegment(sketch, "E34.trimOffspring", {"start": v(-20.75, 10.2) * mm, "end": v(-20.18, 10.2) * mm});
            skLineSegment(sketch, "E35.trimOffspring", {"start": v(-21.1, 10.2) * mm, "end": v(-20.93, 10.75) * mm});
            skLineSegment(sketch, "E36.trimOffspring", {"start": v(-21.22, 9.86) * mm, "end": v(-21.68, 10.2) * mm});
            skLineSegment(sketch, "E37.trimOffspring", {"start": v(-20.64, 9.86) * mm, "end": v(-20.18, 10.2) * mm});
            skLineSegment(sketch, "E38.0.1.0", {"start": v(-20.93, 8) * mm, "end": v(-20.75, 7.46) * mm});
            skLineSegment(sketch, "E38.0.1.1", {"start": v(-20.75, 7.46) * mm, "end": v(-20.18, 7.46) * mm});
            skLineSegment(sketch, "E38.0.1.2", {"start": v(-20.64, 7.12) * mm, "end": v(-20.18, 7.46) * mm});
            skLineSegment(sketch, "E38.0.1.3", {"start": v(-20.64, 7.12) * mm, "end": v(-20.47, 6.57) * mm});
            skLineSegment(sketch, "E38.0.1.4", {"start": v(-20.47, 6.57) * mm, "end": v(-20.93, 6.91) * mm});
            skLineSegment(sketch, "E38.0.1.5", {"start": v(-21.4, 6.57) * mm, "end": v(-20.93, 6.91) * mm});
            skLineSegment(sketch, "E38.0.1.6", {"start": v(-21.4, 6.57) * mm, "end": v(-21.22, 7.12) * mm});
            skLineSegment(sketch, "E38.0.1.7", {"start": v(-21.22, 7.12) * mm, "end": v(-21.68, 7.46) * mm});
            skLineSegment(sketch, "E38.0.1.8", {"start": v(-21.68, 7.46) * mm, "end": v(-21.1, 7.46) * mm});
            skLineSegment(sketch, "E38.0.1.9", {"start": v(-21.1, 7.46) * mm, "end": v(-20.93, 8) * mm});
            skLineSegment(sketch, "E38.0.2.0", {"start": v(-20.93, 5.26) * mm, "end": v(-20.75, 4.71) * mm});
            skLineSegment(sketch, "E38.0.2.1", {"start": v(-20.75, 4.71) * mm, "end": v(-20.18, 4.71) * mm});
            skLineSegment(sketch, "E38.0.2.2", {"start": v(-20.64, 4.38) * mm, "end": v(-20.18, 4.71) * mm});
            skLineSegment(sketch, "E38.0.2.3", {"start": v(-20.64, 4.38) * mm, "end": v(-20.47, 3.83) * mm});
            skLineSegment(sketch, "E38.0.2.4", {"start": v(-20.47, 3.83) * mm, "end": v(-20.93, 4.17) * mm});
            skLineSegment(sketch, "E38.0.2.5", {"start": v(-21.4, 3.83) * mm, "end": v(-20.93, 4.17) * mm});
            skLineSegment(sketch, "E38.0.2.6", {"start": v(-21.4, 3.83) * mm, "end": v(-21.22, 4.38) * mm});
            skLineSegment(sketch, "E38.0.2.7", {"start": v(-21.22, 4.38) * mm, "end": v(-21.68, 4.71) * mm});
            skLineSegment(sketch, "E38.0.2.8", {"start": v(-21.68, 4.71) * mm, "end": v(-21.1, 4.71) * mm});
            skLineSegment(sketch, "E38.0.2.9", {"start": v(-21.1, 4.71) * mm, "end": v(-20.93, 5.26) * mm});
            skLineSegment(sketch, "E38.0.3.0", {"start": v(-20.93, 2.52) * mm, "end": v(-20.75, 1.97) * mm});
            skLineSegment(sketch, "E38.0.3.1", {"start": v(-20.75, 1.97) * mm, "end": v(-20.18, 1.97) * mm});
            skLineSegment(sketch, "E38.0.3.2", {"start": v(-20.64, 1.63) * mm, "end": v(-20.18, 1.97) * mm});
            skLineSegment(sketch, "E38.0.3.3", {"start": v(-20.64, 1.63) * mm, "end": v(-20.47, 1.09) * mm});
            skLineSegment(sketch, "E38.0.3.4", {"start": v(-20.47, 1.09) * mm, "end": v(-20.93, 1.43) * mm});
            skLineSegment(sketch, "E38.0.3.5", {"start": v(-21.4, 1.09) * mm, "end": v(-20.93, 1.43) * mm});
            skLineSegment(sketch, "E38.0.3.6", {"start": v(-21.4, 1.09) * mm, "end": v(-21.22, 1.63) * mm});
            skLineSegment(sketch, "E38.0.3.7", {"start": v(-21.22, 1.63) * mm, "end": v(-21.68, 1.97) * mm});
            skLineSegment(sketch, "E38.0.3.8", {"start": v(-21.68, 1.97) * mm, "end": v(-21.1, 1.97) * mm});
            skLineSegment(sketch, "E38.0.3.9", {"start": v(-21.1, 1.97) * mm, "end": v(-20.93, 2.52) * mm});
            skLineSegment(sketch, "E38.1.0.0", {"start": v(-17.73, 10.75) * mm, "end": v(-17.55, 10.2) * mm});
            skLineSegment(sketch, "E38.1.0.1", {"start": v(-17.55, 10.2) * mm, "end": v(-16.98, 10.2) * mm});
            skLineSegment(sketch, "E38.1.0.2", {"start": v(-17.44, 9.86) * mm, "end": v(-16.98, 10.2) * mm});
            skLineSegment(sketch, "E38.1.0.3", {"start": v(-17.44, 9.86) * mm, "end": v(-17.26, 9.32) * mm});
            skLineSegment(sketch, "E38.1.0.4", {"start": v(-17.26, 9.32) * mm, "end": v(-17.73, 9.66) * mm});
            skLineSegment(sketch, "E38.1.0.5", {"start": v(-18.2, 9.32) * mm, "end": v(-17.73, 9.66) * mm});
            skLineSegment(sketch, "E38.1.0.6", {"start": v(-18.2, 9.32) * mm, "end": v(-18.02, 9.86) * mm});
            skLineSegment(sketch, "E38.1.0.7", {"start": v(-18.02, 9.86) * mm, "end": v(-18.48, 10.2) * mm});
            skLineSegment(sketch, "E38.1.0.8", {"start": v(-18.48, 10.2) * mm, "end": v(-17.9, 10.2) * mm});
            skLineSegment(sketch, "E38.1.0.9", {"start": v(-17.9, 10.2) * mm, "end": v(-17.73, 10.75) * mm});
            skLineSegment(sketch, "E38.1.1.0", {"start": v(-17.73, 8) * mm, "end": v(-17.55, 7.46) * mm});
            skLineSegment(sketch, "E38.1.1.1", {"start": v(-17.55, 7.46) * mm, "end": v(-16.98, 7.46) * mm});
            skLineSegment(sketch, "E38.1.1.2", {"start": v(-17.44, 7.12) * mm, "end": v(-16.98, 7.46) * mm});
            skLineSegment(sketch, "E38.1.1.3", {"start": v(-17.44, 7.12) * mm, "end": v(-17.26, 6.57) * mm});
            skLineSegment(sketch, "E38.1.1.4", {"start": v(-17.26, 6.57) * mm, "end": v(-17.73, 6.91) * mm});
            skLineSegment(sketch, "E38.1.1.5", {"start": v(-18.2, 6.57) * mm, "end": v(-17.73, 6.91) * mm});
            skLineSegment(sketch, "E38.1.1.6", {"start": v(-18.2, 6.57) * mm, "end": v(-18.02, 7.12) * mm});
            skLineSegment(sketch, "E38.1.1.7", {"start": v(-18.02, 7.12) * mm, "end": v(-18.48, 7.46) * mm});
            skLineSegment(sketch, "E38.1.1.8", {"start": v(-18.48, 7.46) * mm, "end": v(-17.9, 7.46) * mm});
            skLineSegment(sketch, "E38.1.1.9", {"start": v(-17.9, 7.46) * mm, "end": v(-17.73, 8) * mm});
            skLineSegment(sketch, "E38.1.2.0", {"start": v(-17.73, 5.26) * mm, "end": v(-17.55, 4.71) * mm});
            skLineSegment(sketch, "E38.1.2.1", {"start": v(-17.55, 4.71) * mm, "end": v(-16.98, 4.71) * mm});
            skLineSegment(sketch, "E38.1.2.2", {"start": v(-17.44, 4.38) * mm, "end": v(-16.98, 4.71) * mm});
            skLineSegment(sketch, "E38.1.2.3", {"start": v(-17.44, 4.38) * mm, "end": v(-17.26, 3.83) * mm});
            skLineSegment(sketch, "E38.1.2.4", {"start": v(-17.26, 3.83) * mm, "end": v(-17.73, 4.17) * mm});
            skLineSegment(sketch, "E38.1.2.5", {"start": v(-18.2, 3.83) * mm, "end": v(-17.73, 4.17) * mm});
            skLineSegment(sketch, "E38.1.2.6", {"start": v(-18.2, 3.83) * mm, "end": v(-18.02, 4.38) * mm});
            skLineSegment(sketch, "E38.1.2.7", {"start": v(-18.02, 4.38) * mm, "end": v(-18.48, 4.71) * mm});
            skLineSegment(sketch, "E38.1.2.8", {"start": v(-18.48, 4.71) * mm, "end": v(-17.9, 4.71) * mm});
            skLineSegment(sketch, "E38.1.2.9", {"start": v(-17.9, 4.71) * mm, "end": v(-17.73, 5.26) * mm});
            skLineSegment(sketch, "E38.1.3.0", {"start": v(-17.73, 2.52) * mm, "end": v(-17.55, 1.97) * mm});
            skLineSegment(sketch, "E38.1.3.1", {"start": v(-17.55, 1.97) * mm, "end": v(-16.98, 1.97) * mm});
            skLineSegment(sketch, "E38.1.3.2", {"start": v(-17.44, 1.63) * mm, "end": v(-16.98, 1.97) * mm});
            skLineSegment(sketch, "E38.1.3.3", {"start": v(-17.44, 1.63) * mm, "end": v(-17.26, 1.09) * mm});
            skLineSegment(sketch, "E38.1.3.4", {"start": v(-17.26, 1.09) * mm, "end": v(-17.73, 1.43) * mm});
            skLineSegment(sketch, "E38.1.3.5", {"start": v(-18.2, 1.09) * mm, "end": v(-17.73, 1.43) * mm});
            skLineSegment(sketch, "E38.1.3.6", {"start": v(-18.2, 1.09) * mm, "end": v(-18.02, 1.63) * mm});
            skLineSegment(sketch, "E38.1.3.7", {"start": v(-18.02, 1.63) * mm, "end": v(-18.48, 1.97) * mm});
            skLineSegment(sketch, "E38.1.3.8", {"start": v(-18.48, 1.97) * mm, "end": v(-17.9, 1.97) * mm});
            skLineSegment(sketch, "E38.1.3.9", {"start": v(-17.9, 1.97) * mm, "end": v(-17.73, 2.52) * mm});
            skLineSegment(sketch, "E38.2.0.0", {"start": v(-14.53, 10.75) * mm, "end": v(-14.35, 10.2) * mm});
            skLineSegment(sketch, "E38.2.0.1", {"start": v(-14.35, 10.2) * mm, "end": v(-13.78, 10.2) * mm});
            skLineSegment(sketch, "E38.2.0.2", {"start": v(-14.24, 9.86) * mm, "end": v(-13.78, 10.2) * mm});
            skLineSegment(sketch, "E38.2.0.3", {"start": v(-14.24, 9.86) * mm, "end": v(-14.06, 9.32) * mm});
            skLineSegment(sketch, "E38.2.0.4", {"start": v(-14.06, 9.32) * mm, "end": v(-14.53, 9.66) * mm});
            skLineSegment(sketch, "E38.2.0.5", {"start": v(-15, 9.32) * mm, "end": v(-14.53, 9.66) * mm});
            skLineSegment(sketch, "E38.2.0.6", {"start": v(-15, 9.32) * mm, "end": v(-14.82, 9.86) * mm});
            skLineSegment(sketch, "E38.2.0.7", {"start": v(-14.82, 9.86) * mm, "end": v(-15.28, 10.2) * mm});
            skLineSegment(sketch, "E38.2.0.8", {"start": v(-15.28, 10.2) * mm, "end": v(-14.7, 10.2) * mm});
            skLineSegment(sketch, "E38.2.0.9", {"start": v(-14.7, 10.2) * mm, "end": v(-14.53, 10.75) * mm});
            skLineSegment(sketch, "E38.2.1.0", {"start": v(-14.53, 8) * mm, "end": v(-14.35, 7.46) * mm});
            skLineSegment(sketch, "E38.2.1.1", {"start": v(-14.35, 7.46) * mm, "end": v(-13.78, 7.46) * mm});
            skLineSegment(sketch, "E38.2.1.2", {"start": v(-14.24, 7.12) * mm, "end": v(-13.78, 7.46) * mm});
            skLineSegment(sketch, "E38.2.1.3", {"start": v(-14.24, 7.12) * mm, "end": v(-14.06, 6.57) * mm});
            skLineSegment(sketch, "E38.2.1.4", {"start": v(-14.06, 6.57) * mm, "end": v(-14.53, 6.91) * mm});
            skLineSegment(sketch, "E38.2.1.5", {"start": v(-15, 6.57) * mm, "end": v(-14.53, 6.91) * mm});
            skLineSegment(sketch, "E38.2.1.6", {"start": v(-15, 6.57) * mm, "end": v(-14.82, 7.12) * mm});
            skLineSegment(sketch, "E38.2.1.7", {"start": v(-14.82, 7.12) * mm, "end": v(-15.28, 7.46) * mm});
            skLineSegment(sketch, "E38.2.1.8", {"start": v(-15.28, 7.46) * mm, "end": v(-14.7, 7.46) * mm});
            skLineSegment(sketch, "E38.2.1.9", {"start": v(-14.7, 7.46) * mm, "end": v(-14.53, 8) * mm});
            skLineSegment(sketch, "E38.2.2.0", {"start": v(-14.53, 5.26) * mm, "end": v(-14.35, 4.71) * mm});
            skLineSegment(sketch, "E38.2.2.1", {"start": v(-14.35, 4.71) * mm, "end": v(-13.78, 4.71) * mm});
            skLineSegment(sketch, "E38.2.2.2", {"start": v(-14.24, 4.38) * mm, "end": v(-13.78, 4.71) * mm});
            skLineSegment(sketch, "E38.2.2.3", {"start": v(-14.24, 4.38) * mm, "end": v(-14.06, 3.83) * mm});
            skLineSegment(sketch, "E38.2.2.4", {"start": v(-14.06, 3.83) * mm, "end": v(-14.53, 4.17) * mm});
            skLineSegment(sketch, "E38.2.2.5", {"start": v(-15, 3.83) * mm, "end": v(-14.53, 4.17) * mm});
            skLineSegment(sketch, "E38.2.2.6", {"start": v(-15, 3.83) * mm, "end": v(-14.82, 4.38) * mm});
            skLineSegment(sketch, "E38.2.2.7", {"start": v(-14.82, 4.38) * mm, "end": v(-15.28, 4.71) * mm});
            skLineSegment(sketch, "E38.2.2.8", {"start": v(-15.28, 4.71) * mm, "end": v(-14.7, 4.71) * mm});
            skLineSegment(sketch, "E38.2.2.9", {"start": v(-14.7, 4.71) * mm, "end": v(-14.53, 5.26) * mm});
            skLineSegment(sketch, "E38.2.3.0", {"start": v(-14.53, 2.52) * mm, "end": v(-14.35, 1.97) * mm});
            skLineSegment(sketch, "E38.2.3.1", {"start": v(-14.35, 1.97) * mm, "end": v(-13.78, 1.97) * mm});
            skLineSegment(sketch, "E38.2.3.2", {"start": v(-14.24, 1.63) * mm, "end": v(-13.78, 1.97) * mm});
            skLineSegment(sketch, "E38.2.3.3", {"start": v(-14.24, 1.63) * mm, "end": v(-14.06, 1.09) * mm});
            skLineSegment(sketch, "E38.2.3.4", {"start": v(-14.06, 1.09) * mm, "end": v(-14.53, 1.43) * mm});
            skLineSegment(sketch, "E38.2.3.5", {"start": v(-15, 1.09) * mm, "end": v(-14.53, 1.43) * mm});
            skLineSegment(sketch, "E38.2.3.6", {"start": v(-15, 1.09) * mm, "end": v(-14.82, 1.63) * mm});
            skLineSegment(sketch, "E38.2.3.7", {"start": v(-14.82, 1.63) * mm, "end": v(-15.28, 1.97) * mm});
            skLineSegment(sketch, "E38.2.3.8", {"start": v(-15.28, 1.97) * mm, "end": v(-14.7, 1.97) * mm});
            skLineSegment(sketch, "E38.2.3.9", {"start": v(-14.7, 1.97) * mm, "end": v(-14.53, 2.52) * mm});
            skLineSegment(sketch, "E38.3.0.0", {"start": v(-11.33, 10.75) * mm, "end": v(-11.15, 10.2) * mm});
            skLineSegment(sketch, "E38.3.0.1", {"start": v(-11.15, 10.2) * mm, "end": v(-10.58, 10.2) * mm});
            skLineSegment(sketch, "E38.3.0.2", {"start": v(-11.04, 9.86) * mm, "end": v(-10.58, 10.2) * mm});
            skLineSegment(sketch, "E38.3.0.3", {"start": v(-11.04, 9.86) * mm, "end": v(-10.86, 9.32) * mm});
            skLineSegment(sketch, "E38.3.0.4", {"start": v(-10.86, 9.32) * mm, "end": v(-11.33, 9.66) * mm});
            skLineSegment(sketch, "E38.3.0.5", {"start": v(-11.8, 9.32) * mm, "end": v(-11.33, 9.66) * mm});
            skLineSegment(sketch, "E38.3.0.6", {"start": v(-11.8, 9.32) * mm, "end": v(-11.62, 9.86) * mm});
            skLineSegment(sketch, "E38.3.0.7", {"start": v(-11.62, 9.86) * mm, "end": v(-12.08, 10.2) * mm});
            skLineSegment(sketch, "E38.3.0.8", {"start": v(-12.08, 10.2) * mm, "end": v(-11.5, 10.2) * mm});
            skLineSegment(sketch, "E38.3.0.9", {"start": v(-11.5, 10.2) * mm, "end": v(-11.33, 10.75) * mm});
            skLineSegment(sketch, "E38.3.1.0", {"start": v(-11.33, 8) * mm, "end": v(-11.15, 7.46) * mm});
            skLineSegment(sketch, "E38.3.1.1", {"start": v(-11.15, 7.46) * mm, "end": v(-10.58, 7.46) * mm});
            skLineSegment(sketch, "E38.3.1.2", {"start": v(-11.04, 7.12) * mm, "end": v(-10.58, 7.46) * mm});
            skLineSegment(sketch, "E38.3.1.3", {"start": v(-11.04, 7.12) * mm, "end": v(-10.86, 6.57) * mm});
            skLineSegment(sketch, "E38.3.1.4", {"start": v(-10.86, 6.57) * mm, "end": v(-11.33, 6.91) * mm});
            skLineSegment(sketch, "E38.3.1.5", {"start": v(-11.8, 6.57) * mm, "end": v(-11.33, 6.91) * mm});
            skLineSegment(sketch, "E38.3.1.6", {"start": v(-11.8, 6.57) * mm, "end": v(-11.62, 7.12) * mm});
            skLineSegment(sketch, "E38.3.1.7", {"start": v(-11.62, 7.12) * mm, "end": v(-12.08, 7.46) * mm});
            skLineSegment(sketch, "E38.3.1.8", {"start": v(-12.08, 7.46) * mm, "end": v(-11.5, 7.46) * mm});
            skLineSegment(sketch, "E38.3.1.9", {"start": v(-11.5, 7.46) * mm, "end": v(-11.33, 8) * mm});
            skLineSegment(sketch, "E38.3.2.0", {"start": v(-11.33, 5.26) * mm, "end": v(-11.15, 4.71) * mm});
            skLineSegment(sketch, "E38.3.2.1", {"start": v(-11.15, 4.71) * mm, "end": v(-10.58, 4.71) * mm});
            skLineSegment(sketch, "E38.3.2.2", {"start": v(-11.04, 4.38) * mm, "end": v(-10.58, 4.71) * mm});
            skLineSegment(sketch, "E38.3.2.3", {"start": v(-11.04, 4.38) * mm, "end": v(-10.86, 3.83) * mm});
            skLineSegment(sketch, "E38.3.2.4", {"start": v(-10.86, 3.83) * mm, "end": v(-11.33, 4.17) * mm});
            skLineSegment(sketch, "E38.3.2.5", {"start": v(-11.8, 3.83) * mm, "end": v(-11.33, 4.17) * mm});
            skLineSegment(sketch, "E38.3.2.6", {"start": v(-11.8, 3.83) * mm, "end": v(-11.62, 4.38) * mm});
            skLineSegment(sketch, "E38.3.2.7", {"start": v(-11.62, 4.38) * mm, "end": v(-12.08, 4.71) * mm});
            skLineSegment(sketch, "E38.3.2.8", {"start": v(-12.08, 4.71) * mm, "end": v(-11.5, 4.71) * mm});
            skLineSegment(sketch, "E38.3.2.9", {"start": v(-11.5, 4.71) * mm, "end": v(-11.33, 5.26) * mm});
            skLineSegment(sketch, "E38.3.3.0", {"start": v(-11.33, 2.52) * mm, "end": v(-11.15, 1.97) * mm});
            skLineSegment(sketch, "E38.3.3.1", {"start": v(-11.15, 1.97) * mm, "end": v(-10.58, 1.97) * mm});
            skLineSegment(sketch, "E38.3.3.2", {"start": v(-11.04, 1.63) * mm, "end": v(-10.58, 1.97) * mm});
            skLineSegment(sketch, "E38.3.3.3", {"start": v(-11.04, 1.63) * mm, "end": v(-10.86, 1.09) * mm});
            skLineSegment(sketch, "E38.3.3.4", {"start": v(-10.86, 1.09) * mm, "end": v(-11.33, 1.43) * mm});
            skLineSegment(sketch, "E38.3.3.5", {"start": v(-11.8, 1.09) * mm, "end": v(-11.33, 1.43) * mm});
            skLineSegment(sketch, "E38.3.3.6", {"start": v(-11.8, 1.09) * mm, "end": v(-11.62, 1.63) * mm});
            skLineSegment(sketch, "E38.3.3.7", {"start": v(-11.62, 1.63) * mm, "end": v(-12.08, 1.97) * mm});
            skLineSegment(sketch, "E38.3.3.8", {"start": v(-12.08, 1.97) * mm, "end": v(-11.5, 1.97) * mm});
            skLineSegment(sketch, "E38.3.3.9", {"start": v(-11.5, 1.97) * mm, "end": v(-11.33, 2.52) * mm});
            skLineSegment(sketch, "E38.4.0.0", {"start": v(-8.13, 10.75) * mm, "end": v(-7.95, 10.2) * mm});
            skLineSegment(sketch, "E38.4.0.1", {"start": v(-7.95, 10.2) * mm, "end": v(-7.38, 10.2) * mm});
            skLineSegment(sketch, "E38.4.0.2", {"start": v(-7.84, 9.86) * mm, "end": v(-7.38, 10.2) * mm});
            skLineSegment(sketch, "E38.4.0.3", {"start": v(-7.84, 9.86) * mm, "end": v(-7.66, 9.32) * mm});
            skLineSegment(sketch, "E38.4.0.4", {"start": v(-7.66, 9.32) * mm, "end": v(-8.13, 9.66) * mm});
            skLineSegment(sketch, "E38.4.0.5", {"start": v(-8.6, 9.32) * mm, "end": v(-8.13, 9.66) * mm});
            skLineSegment(sketch, "E38.4.0.6", {"start": v(-8.6, 9.32) * mm, "end": v(-8.41, 9.86) * mm});
            skLineSegment(sketch, "E38.4.0.7", {"start": v(-8.41, 9.86) * mm, "end": v(-8.88, 10.2) * mm});
            skLineSegment(sketch, "E38.4.0.8", {"start": v(-8.88, 10.2) * mm, "end": v(-8.3, 10.2) * mm});
            skLineSegment(sketch, "E38.4.0.9", {"start": v(-8.3, 10.2) * mm, "end": v(-8.13, 10.75) * mm});
            skLineSegment(sketch, "E38.4.1.0", {"start": v(-8.13, 8) * mm, "end": v(-7.95, 7.46) * mm});
            skLineSegment(sketch, "E38.4.1.1", {"start": v(-7.95, 7.46) * mm, "end": v(-7.38, 7.46) * mm});
            skLineSegment(sketch, "E38.4.1.2", {"start": v(-7.84, 7.12) * mm, "end": v(-7.38, 7.46) * mm});
            skLineSegment(sketch, "E38.4.1.3", {"start": v(-7.84, 7.12) * mm, "end": v(-7.66, 6.57) * mm});
            skLineSegment(sketch, "E38.4.1.4", {"start": v(-7.66, 6.57) * mm, "end": v(-8.13, 6.91) * mm});
            skLineSegment(sketch, "E38.4.1.5", {"start": v(-8.6, 6.57) * mm, "end": v(-8.13, 6.91) * mm});
            skLineSegment(sketch, "E38.4.1.6", {"start": v(-8.6, 6.57) * mm, "end": v(-8.41, 7.12) * mm});
            skLineSegment(sketch, "E38.4.1.7", {"start": v(-8.41, 7.12) * mm, "end": v(-8.88, 7.46) * mm});
            skLineSegment(sketch, "E38.4.1.8", {"start": v(-8.88, 7.46) * mm, "end": v(-8.3, 7.46) * mm});
            skLineSegment(sketch, "E38.4.1.9", {"start": v(-8.3, 7.46) * mm, "end": v(-8.13, 8) * mm});
            skLineSegment(sketch, "E38.4.2.0", {"start": v(-8.13, 5.26) * mm, "end": v(-7.95, 4.71) * mm});
            skLineSegment(sketch, "E38.4.2.1", {"start": v(-7.95, 4.71) * mm, "end": v(-7.38, 4.71) * mm});
            skLineSegment(sketch, "E38.4.2.2", {"start": v(-7.84, 4.38) * mm, "end": v(-7.38, 4.71) * mm});
            skLineSegment(sketch, "E38.4.2.3", {"start": v(-7.84, 4.38) * mm, "end": v(-7.66, 3.83) * mm});
            skLineSegment(sketch, "E38.4.2.4", {"start": v(-7.66, 3.83) * mm, "end": v(-8.13, 4.17) * mm});
            skLineSegment(sketch, "E38.4.2.5", {"start": v(-8.6, 3.83) * mm, "end": v(-8.13, 4.17) * mm});
            skLineSegment(sketch, "E38.4.2.6", {"start": v(-8.6, 3.83) * mm, "end": v(-8.41, 4.38) * mm});
            skLineSegment(sketch, "E38.4.2.7", {"start": v(-8.41, 4.38) * mm, "end": v(-8.88, 4.71) * mm});
            skLineSegment(sketch, "E38.4.2.8", {"start": v(-8.88, 4.71) * mm, "end": v(-8.3, 4.71) * mm});
            skLineSegment(sketch, "E38.4.2.9", {"start": v(-8.3, 4.71) * mm, "end": v(-8.13, 5.26) * mm});
            skLineSegment(sketch, "E38.4.3.0", {"start": v(-8.13, 2.52) * mm, "end": v(-7.95, 1.97) * mm});
            skLineSegment(sketch, "E38.4.3.1", {"start": v(-7.95, 1.97) * mm, "end": v(-7.38, 1.97) * mm});
            skLineSegment(sketch, "E38.4.3.2", {"start": v(-7.84, 1.63) * mm, "end": v(-7.38, 1.97) * mm});
            skLineSegment(sketch, "E38.4.3.3", {"start": v(-7.84, 1.63) * mm, "end": v(-7.66, 1.09) * mm});
            skLineSegment(sketch, "E38.4.3.4", {"start": v(-7.66, 1.09) * mm, "end": v(-8.13, 1.43) * mm});
            skLineSegment(sketch, "E38.4.3.5", {"start": v(-8.6, 1.09) * mm, "end": v(-8.13, 1.43) * mm});
            skLineSegment(sketch, "E38.4.3.6", {"start": v(-8.6, 1.09) * mm, "end": v(-8.41, 1.63) * mm});
            skLineSegment(sketch, "E38.4.3.7", {"start": v(-8.41, 1.63) * mm, "end": v(-8.88, 1.97) * mm});
            skLineSegment(sketch, "E38.4.3.8", {"start": v(-8.88, 1.97) * mm, "end": v(-8.3, 1.97) * mm});
            skLineSegment(sketch, "E38.4.3.9", {"start": v(-8.3, 1.97) * mm, "end": v(-8.13, 2.52) * mm});
            skLineSegment(sketch, "E38.direction1", {"start": v(-20.75, 10.2) * mm, "end": v(-17.55, 10.2) * mm, "construction": true});
            skLineSegment(sketch, "E38.direction2", {"start": v(-20.75, 10.2) * mm, "end": v(-20.75, 7.46) * mm, "construction": true});
            skSolve(sketch);
        }
        {
            var Q0;
            Q0=makeQuery(id+"F0.imprint","IMPRINT",FACE,{"disambiguationData":[TD([[makeQuery(id+"F0.imprint","IMPRINT",EDGE,{"derivedFrom":sQuery(id+"F0.wireOp",EDGE,"E2.bottom")}),-1.0]])]});
            var Q1;
            {var subQ0=sQuery(id+"F0.wireOp",EDGE,"E3.MirrorCS");Q1=makeQuery(id+"F0.imprint","IMPRINT",FACE,{"disambiguationData":[TD([[makeQuery(id+"F0.imprint","IMPRINT",EDGE,{"derivedFrom":subQ0}),-1.0]])]});}
            var Q2;
            {var subQ0=sQuery(id+"F0.wireOp",EDGE,"E5.MirrorCS");Q2=makeQuery(id+"F0.imprint","IMPRINT",FACE,{"disambiguationData":[TD([[makeQuery(id+"F0.imprint","IMPRINT",EDGE,{"derivedFrom":subQ0}),-1.0]])]});}
            var Q3;
            {var subQ0=sQuery(id+"F0.wireOp",EDGE,"E7.MirrorCS");Q3=makeQuery(id+"F0.imprint","IMPRINT",FACE,{"disambiguationData":[TD([[makeQuery(id+"F0.imprint","IMPRINT",EDGE,{"derivedFrom":subQ0}),-1.0]])]});}
            var Q4;
            {var subQ0=sQuery(id+"F0.wireOp",EDGE,"E9.top");Q4=makeQuery(id+"F0.imprint","IMPRINT",FACE,{"disambiguationData":[TD([[makeQuery(id+"F0.imprint","IMPRINT",EDGE,{"derivedFrom":subQ0}),-1.0]])]});}
            var Q5;
            {var subQ0=sQuery(id+"F0.wireOp",EDGE,"E11.MirrorCS");Q5=makeQuery(id+"F0.imprint","IMPRINT",FACE,{"disambiguationData":[TD([[makeQuery(id+"F0.imprint","IMPRINT",EDGE,{"derivedFrom":subQ0}),-1.0]])]});}
            var Q6;
            {var subQ0=sQuery(id+"F0.wireOp",EDGE,"E0.rect.top");Q6=makeQuery(id+"F0.imprint","IMPRINT",FACE,{"disambiguationData":[TD([[makeQuery(id+"F0.imprint","IMPRINT",EDGE,{"derivedFrom":subQ0}),-1.0]])]});}
            extrude(context, id + "F1", {"entities" : qUnion([Q0, Q1, Q2, Q3, Q4, Q5, Q6]), "depth" : 2 * mm, "offsetDistance" : 25.4 * mm});
        }
        {
            var Q0;
            Q0=qCreatedBy(makeId("Top.planeOp"),FACE);
            var sketch = newSketch(context, id + "F2", { "sketchPlane" : qUnion([Q0])});
            skLineSegment(sketch, "E39.bottom", {"start": v(28.58, 15.88) * mm, "end": v(-28.57, 15.88) * mm});
            skLineSegment(sketch, "E39.top", {"start": v(28.57, -15.88) * mm, "end": v(-28.58, -15.88) * mm});
            skLineSegment(sketch, "E39.left", {"start": v(28.58, 15.88) * mm, "end": v(28.57, -15.87) * mm});
            skLineSegment(sketch, "E39.right", {"start": v(-28.57, 15.88) * mm, "end": v(-28.58, -15.88) * mm});
            skPoint(sketch, "E39.middle", {"position": v(0, 0) * mm});
            skLineSegment(sketch, "E40.0", {"start": v(28.83, 16.13) * mm, "end": v(-28.83, 16.13) * mm});
            skLineSegment(sketch, "E40.1", {"start": v(28.83, 16.13) * mm, "end": v(28.83, -16.13) * mm});
            skLineSegment(sketch, "E40.2", {"start": v(28.83, -16.13) * mm, "end": v(-28.83, -16.13) * mm});
            skLineSegment(sketch, "E40.3", {"start": v(-28.83, 16.13) * mm, "end": v(-28.83, -16.13) * mm});
            skSolve(sketch);
        }
        {
            var Q0;
            Q0=qSketchRegion(id+"F2",true);
            extrude(context, id + "F3", {"entities" : qUnion([Q0]), "depth" : 2 * mm, "offsetDistance" : 25.4 * mm});
        }
        {
            var Q0;
            Q0=qCreatedBy(makeId("Top.planeOp"),FACE);
            var sketch = newSketch(context, id + "F4", { "sketchPlane" : qUnion([Q0])});
            skLineSegment(sketch, "E41.bottom", {"start": v(28.58, 15.88) * mm, "end": v(-28.57, 15.88) * mm});
            skLineSegment(sketch, "E41.top", {"start": v(28.57, -15.88) * mm, "end": v(-28.58, -15.88) * mm});
            skLineSegment(sketch, "E41.left", {"start": v(28.58, 15.88) * mm, "end": v(28.57, -15.88) * mm});
            skLineSegment(sketch, "E41.right", {"start": v(-28.57, 15.88) * mm, "end": v(-28.58, -15.88) * mm});
            skPoint(sketch, "E41.middle", {"position": v(0, 0) * mm});
            skSolve(sketch);
        }
        {
            var Q0;
            Q0=qSketchRegion(id+"F4",true);
            extrude(context, id + "F5", {"entities" : qUnion([Q0]), "depth" : .5 * mm, "offsetDistance" : 25.4 * mm});
        }
    });
